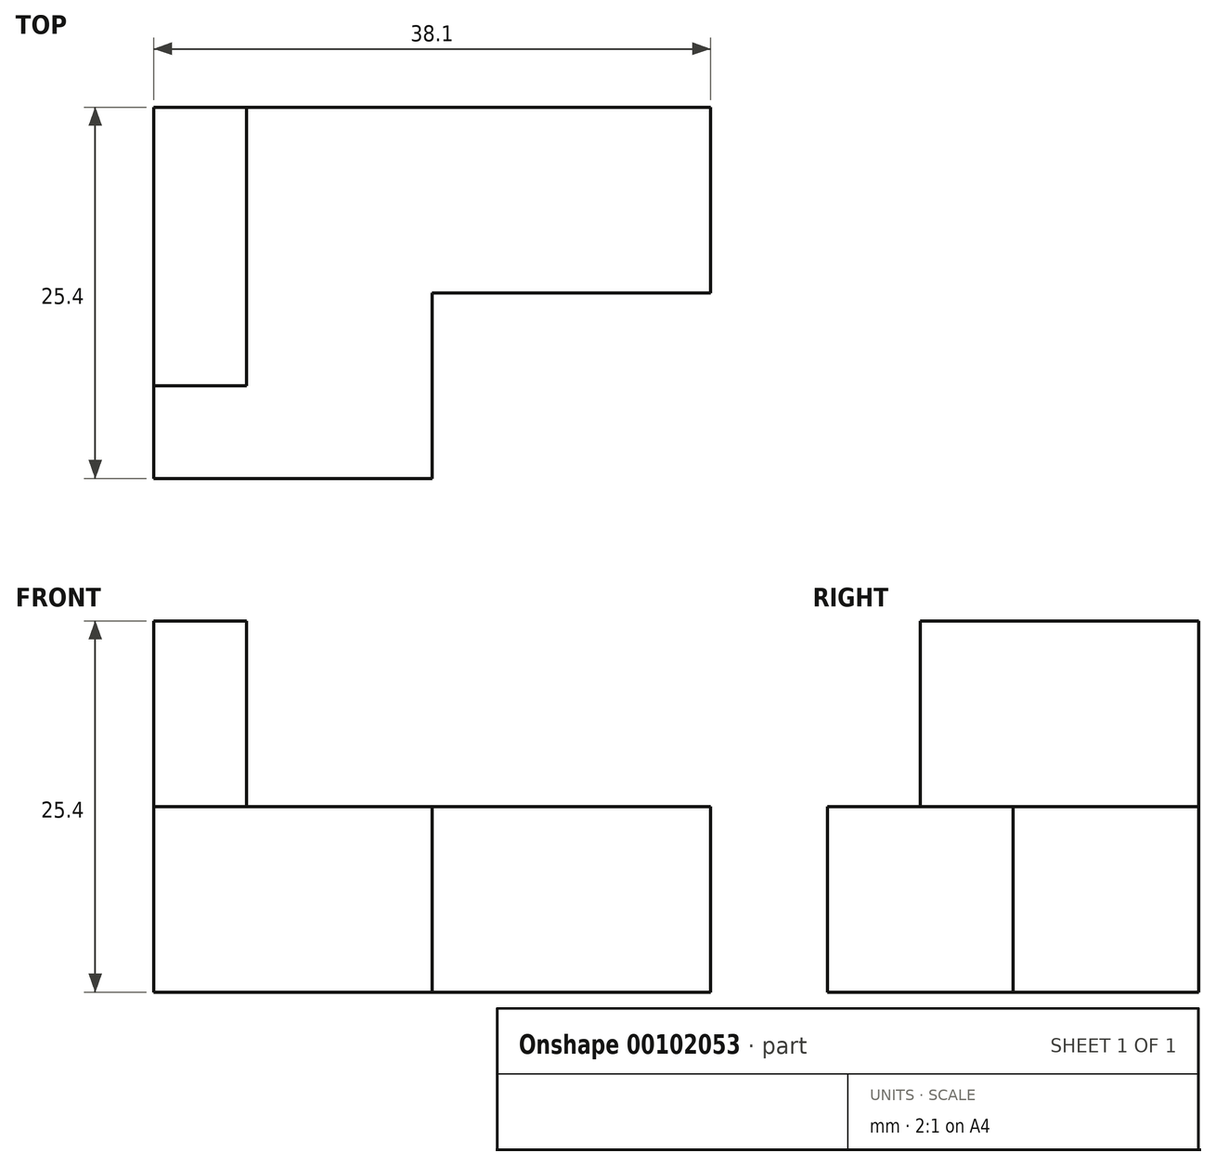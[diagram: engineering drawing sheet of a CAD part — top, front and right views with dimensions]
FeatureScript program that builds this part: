
annotation { "Feature Type Name" : "Feature", "Feature Type Description" : "" }
export const myFeature = defineFeature(function(context is Context, id is Id, definition is map)
    precondition{}
    {
        {
            var Q0;
            Q0=qCreatedBy(makeId("Front.planeOp"),FACE);
            var sketch = newSketch(context, id + "F0", { "sketchPlane" : qUnion([Q0])});
            skLineSegment(sketch, "E0.bottom", {"start": v(0, 0) * mm, "end": v(19.05, 0) * mm});
            skLineSegment(sketch, "E0.top", {"start": v(0, 12.7) * mm, "end": v(19.05, 12.7) * mm});
            skLineSegment(sketch, "E0.left", {"start": v(0, 0) * mm, "end": v(0, 12.7) * mm});
            skLineSegment(sketch, "E0.right", {"start": v(19.05, 0) * mm, "end": v(19.05, 12.7) * mm});
            skLineSegment(sketch, "E1.bottom", {"start": v(19.05, 12.7) * mm, "end": v(38.1, 12.7) * mm});
            skLineSegment(sketch, "E1.top", {"start": v(19.05, 0) * mm, "end": v(38.1, 0) * mm});
            skLineSegment(sketch, "E1.left", {"start": v(19.05, 12.7) * mm, "end": v(19.05, 0) * mm});
            skLineSegment(sketch, "E1.right", {"start": v(38.1, 12.7) * mm, "end": v(38.1, 0) * mm});
            skSolve(sketch);
        }
        {
            var Q0;
            Q0=makeQuery(id+"F0.imprint","IMPRINT",FACE,{"disambiguationData":[TD([[makeQuery(id+"F0.imprint","IMPRINT",EDGE,{"derivedFrom":sQuery(id+"F0.wireOp",EDGE,"E0.bottom")}),1.0]])]});
            extrude(context, id + "F1", {"entities" : qUnion([Q0]), "depth" : 25.4 * mm});
        }
        {
            var Q0;
            Q0=makeQuery(id+"F0.imprint","IMPRINT",FACE,{"disambiguationData":[TD([[makeQuery(id+"F0.imprint","IMPRINT",EDGE,{"derivedFrom":sQuery(id+"F0.wireOp",EDGE,"E1.bottom")}),-1.0]])]});
            extrude(context, id + "F2", {"entities" : qUnion([Q0]), "operationType" : NewBodyOperationType.ADD, "depth" : 12.7 * mm});
        }
        {
            var Q0;
            Q0=qCreatedBy(makeId("Right.planeOp"),FACE);
            var sketch = newSketch(context, id + "F3", { "sketchPlane" : qUnion([Q0])});
            skLineSegment(sketch, "E2.bottom", {"start": v(0, 0) * mm, "end": v(-19.05, 0) * mm});
            skLineSegment(sketch, "E2.top", {"start": v(0, 25.4) * mm, "end": v(-19.05, 25.4) * mm});
            skLineSegment(sketch, "E2.left", {"start": v(0, 0) * mm, "end": v(0, 25.4) * mm});
            skLineSegment(sketch, "E2.right", {"start": v(-19.05, 0) * mm, "end": v(-19.05, 25.4) * mm});
            skSolve(sketch);
        }
        {
            var Q0;
            Q0=makeQuery(id+"F3.imprint","IMPRINT",FACE,{"disambiguationData":[TD([[makeQuery(id+"F3.imprint","IMPRINT",EDGE,{"derivedFrom":sQuery(id+"F3.wireOp",EDGE,"E2.bottom")}),-1.0]])]});
            extrude(context, id + "F4", {"entities" : qUnion([Q0]), "operationType" : NewBodyOperationType.ADD, "depth" : 6.35 * mm});
        }
    });
